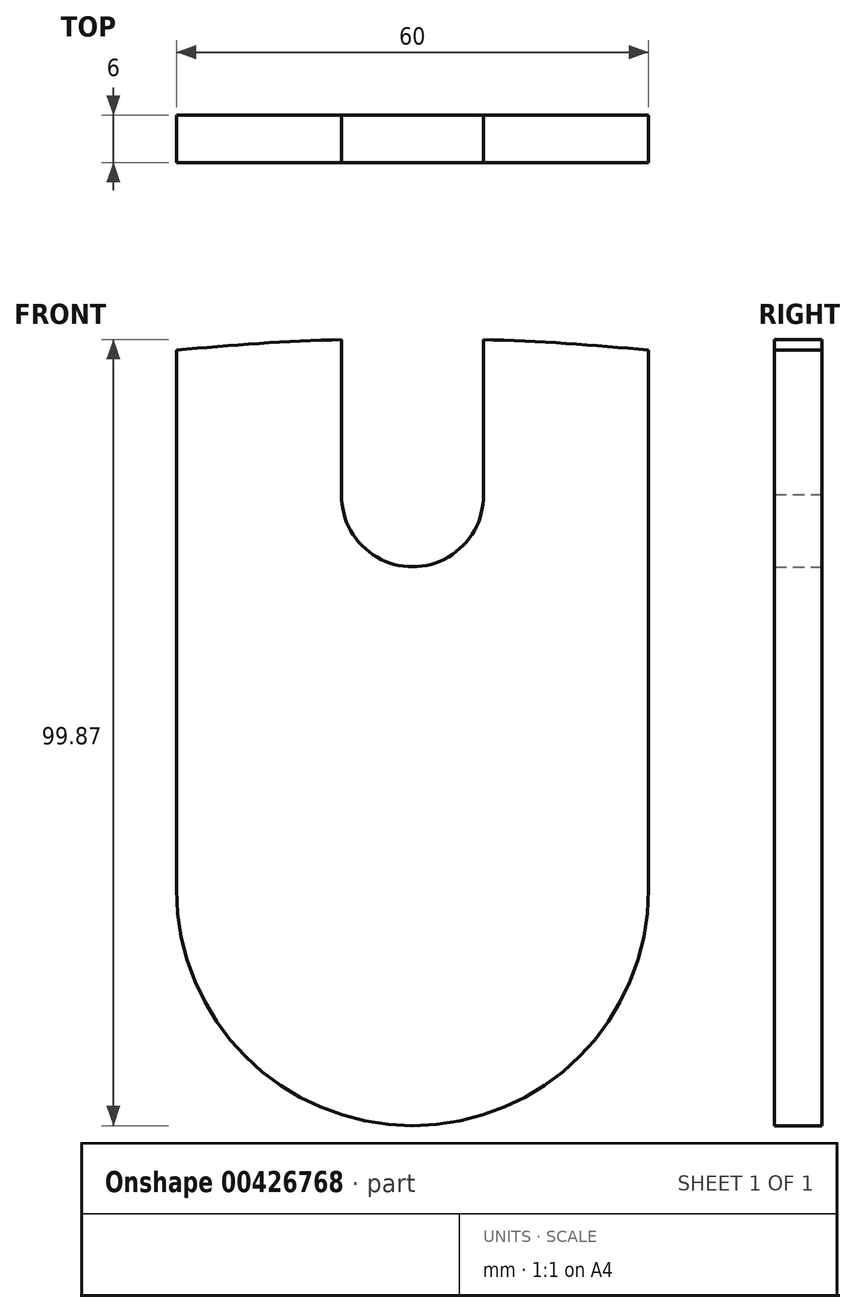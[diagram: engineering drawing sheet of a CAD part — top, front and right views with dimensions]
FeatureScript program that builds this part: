
annotation { "Feature Type Name" : "Feature", "Feature Type Description" : "" }
export const myFeature = defineFeature(function(context is Context, id is Id, definition is map)
    precondition{}
    {
        {
            var Q0;
            Q0=qCreatedBy(makeId("Front.planeOp"),FACE);
            var sketch = newSketch(context, id + "F0", { "sketchPlane" : qUnion([Q0])});
            skCircle(sketch, "E0", {"center": v(0, -280) * mm, "radius": 280 * mm, "construction": true});
            skCircle(sketch, "E1", {"center": v(0, 0) * mm, "radius": 9 * mm});
            skLineSegment(sketch, "E2", {"start": v(-9, -0.14) * mm, "end": v(-9, 19.87) * mm});
            skLineSegment(sketch, "E3", {"start": v(9, -0.14) * mm, "end": v(9, 19.87) * mm});
            skCircle(sketch, "E4", {"center": v(0, -50) * mm, "radius": 30 * mm});
            skLineSegment(sketch, "E5", {"start": v(-30, -50) * mm, "end": v(-30, 18.5) * mm});
            skLineSegment(sketch, "E6", {"start": v(30, -50) * mm, "end": v(30, 18.5) * mm});
            skLineSegment(sketch, "E7", {"start": v(-30, 18.5) * mm, "end": v(-30, 18.5) * mm});
            skArc(sketch, "E8", {"start": v(30, 18.5) * mm, "mid": v(0, 20) * mm, "end": v(-30, 18.5) * mm});
            skArc(sketch, "E9", {"start": v(-30, 18.5) * mm, "mid": v(0, -580) * mm, "end": v(30, 18.5) * mm, "construction": true});
            skSolve(sketch);
        }
        {
            var Q0;
            {var subQ8=sQuery(id+"F0.wireOp",EDGE,"E5");Q0=makeQuery(id+"F0.imprint","IMPRINT",FACE,{"disambiguationData":[TD([[makeQuery(id+"F0.imprint","IMPRINT",EDGE,{"derivedFrom":subQ8}),-1.0]])]});}
            var Q1;
            {var subQ0=sQuery(id+"F0.wireOp",EDGE,"E4");var subQ1=makeQuery(id+"F0.imprint","INTERSECT",VERTEX,{"derivedFrom":[subQ0,sQuery(id+"F0.wireOp",EDGE,"E5")]});Q1=makeQuery(id+"F0.imprint","IMPRINT",FACE,{"disambiguationData":[TD([[makeQuery(id+"F0.imprint","IMPRINT",EDGE,{"disambiguationData":[TD([[subQ1,1.0]])],"derivedFrom":subQ0}),1.0]])]});}
            extrude(context, id + "F1", {"entities" : qUnion([Q0, Q1]), "depth" : 6 * mm});
        }
    });
